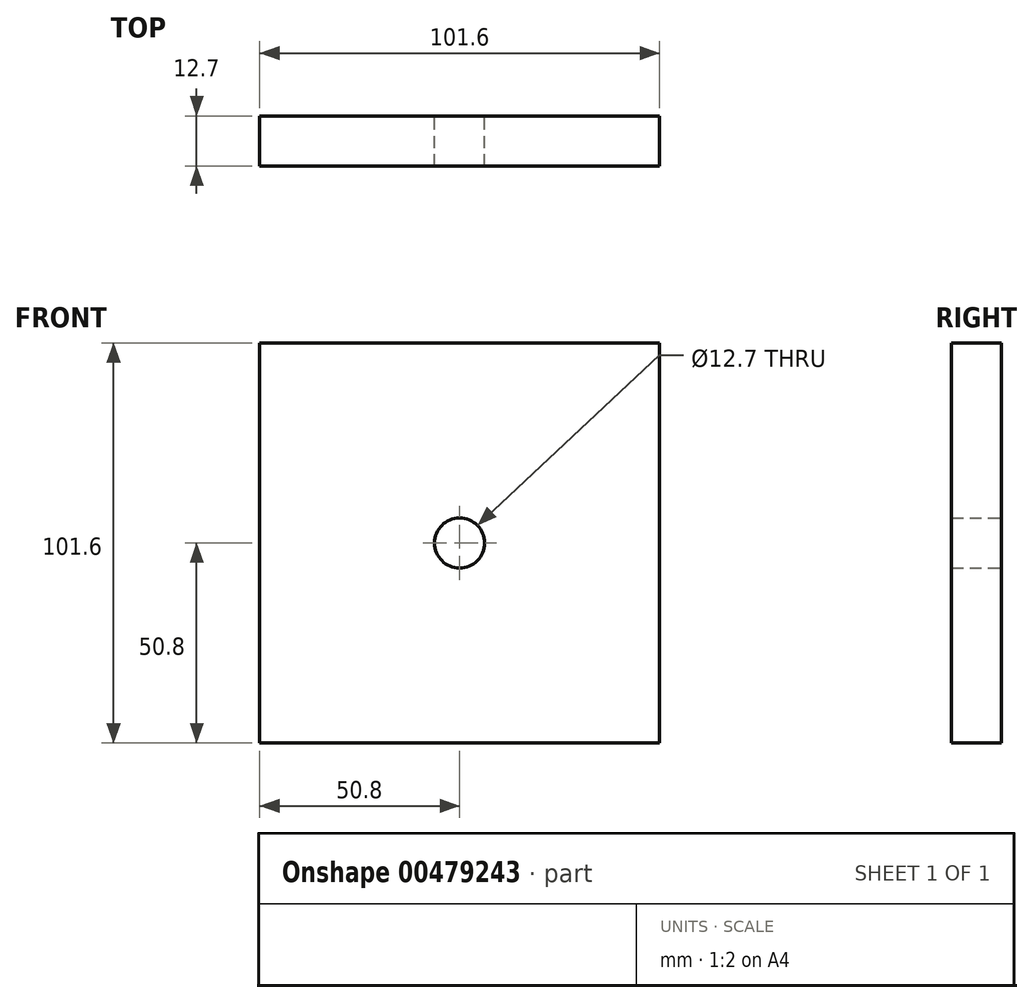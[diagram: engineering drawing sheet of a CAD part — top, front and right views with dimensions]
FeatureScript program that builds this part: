
annotation { "Feature Type Name" : "Feature", "Feature Type Description" : "" }
export const myFeature = defineFeature(function(context is Context, id is Id, definition is map)
    precondition{}
    {
        {
            var Q0;
            Q0=qCreatedBy(makeId("Front.planeOp"),FACE);
            var sketch = newSketch(context, id + "F0", { "sketchPlane" : qUnion([Q0])});
            skLineSegment(sketch, "E0.bottom", {"start": v(50.8, 50.8) * mm, "end": v(-50.8, 50.8) * mm});
            skLineSegment(sketch, "E0.top", {"start": v(50.8, -50.8) * mm, "end": v(-50.8, -50.8) * mm});
            skLineSegment(sketch, "E0.left", {"start": v(50.8, 50.8) * mm, "end": v(50.8, -50.8) * mm});
            skLineSegment(sketch, "E0.right", {"start": v(-50.8, 50.8) * mm, "end": v(-50.8, -50.8) * mm});
            skPoint(sketch, "E0.middle", {"position": v(0, 0) * mm});
            skSolve(sketch);
        }
        {
            var Q0;
            Q0 = qSketchRegion(id + "F0", true);
            extrude(context, id + "F1", {"entities" : qUnion([Q0]), "oppositeDirection" : true, "depth" : 12.7 * mm});
        }
        {
            var Q0;
            Q0=makeQuery(id+"F1.opExtrude","CAP_FACE",FACE,{"disambiguationData":[OSD([sQuery(id+"F0.wireOp",EDGE,"E0.bottom"),sQuery(id+"F0.wireOp",EDGE,"E0.top"),sQuery(id+"F0.wireOp",EDGE,"E0.left"),sQuery(id+"F0.wireOp",EDGE,"E0.right")])],"isStart":false});
            var sketch = newSketch(context, id + "F2", { "sketchPlane" : qUnion([Q0])});
            skCircle(sketch, "E1", {"center": v(0, 0) * mm, "radius": 38.1 * mm});
            skCircle(sketch, "E2", {"center": v(0, 0) * mm, "radius": 15.24 * mm});
            skCircle(sketch, "E3", {"center": v(0, 0) * mm, "radius": 6.35 * mm});
            skSolve(sketch);
        }
        {
            var Q0;
            Q0=makeQuery(id+"F2.imprint","IMPRINT",FACE,{"disambiguationData":[TD([[makeQuery(id+"F2.imprint","IMPRINT",EDGE,{"derivedFrom":sQuery(id+"F2.wireOp",EDGE,"E3")}),1.0]])]});
            extrude(context, id + "F3", {"entities" : qUnion([Q0]), "operationType" : NewBodyOperationType.REMOVE, "endBound" : BoundingType.THROUGH_ALL, "oppositeDirection" : true, "depth" : 25.4 * mm});
        }
    });
